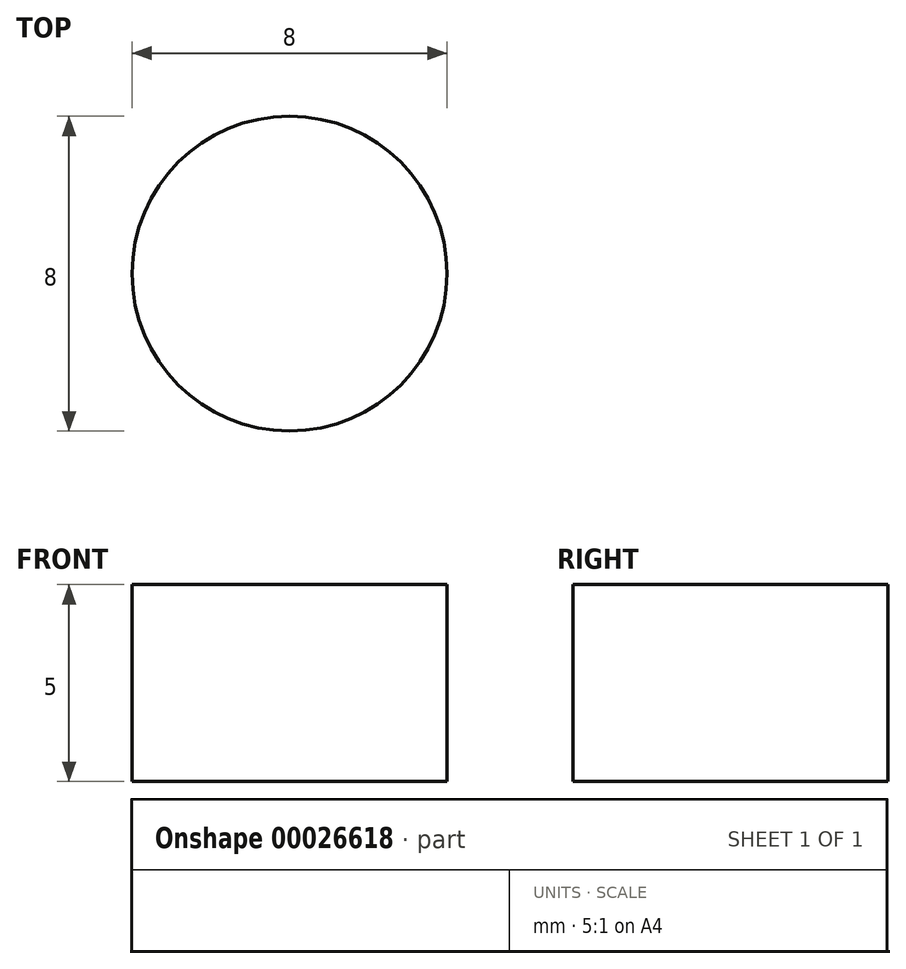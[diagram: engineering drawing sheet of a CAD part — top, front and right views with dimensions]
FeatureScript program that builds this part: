
annotation { "Feature Type Name" : "Feature", "Feature Type Description" : "" }
export const myFeature = defineFeature(function(context is Context, id is Id, definition is map)
    precondition{}
    {
        {
            var Q0;
            Q0=qCreatedBy(makeId("Top.planeOp"),FACE);
            var sketch = newSketch(context, id + "F0", { "sketchPlane" : qUnion([Q0])});
            skCircle(sketch, "E0", {"center": v(0, 0) * mm, "radius": 4 * mm});
            skSolve(sketch);
        }
        {
            var Q0;
            Q0 = qSketchRegion(id + "F0", true);
            extrude(context, id + "F1", {"entities" : qUnion([Q0]), "depth" : 5 * mm});
        }
    });
